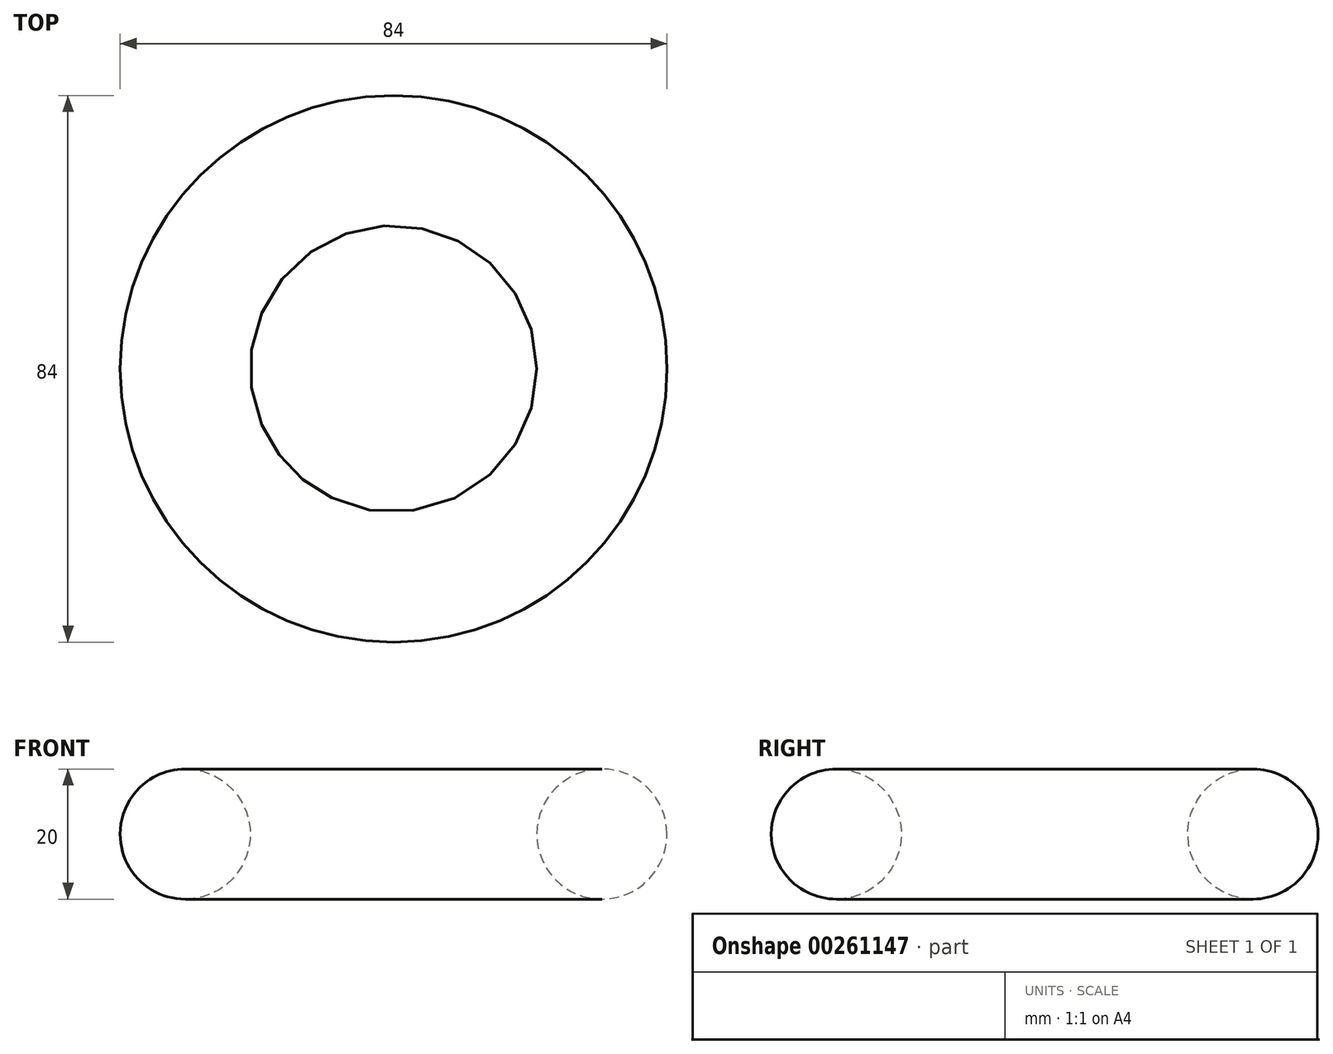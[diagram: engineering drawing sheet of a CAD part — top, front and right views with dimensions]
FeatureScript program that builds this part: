
annotation { "Feature Type Name" : "Feature", "Feature Type Description" : "" }
export const myFeature = defineFeature(function(context is Context, id is Id, definition is map)
    precondition{}
    {
        {
            var Q0;
            Q0=qCreatedBy(makeId("Front.planeOp"),FACE);
            var sketch = newSketch(context, id + "F0", { "sketchPlane" : qUnion([Q0])});
            skCircle(sketch, "E0", {"center": v(32, 0) * mm, "radius": 10 * mm});
            skLineSegment(sketch, "E1", {"start": v(0, 39.73) * mm, "end": v(0, -48.34) * mm, "construction": true});
            skSolve(sketch);
        }
        {
            var Q0;
            Q0=makeQuery(id+"F0.imprint","IMPRINT",FACE,{"disambiguationData":[TD([[makeQuery(id+"F0.imprint","IMPRINT",EDGE,{"derivedFrom":sQuery(id+"F0.wireOp",EDGE,"E0")}),1.0]])]});
            var Q1;
            Q1=sQuery(id+"F0.wireOp",EDGE,"E1");
            revolve(context, id + "F1", {"entities" : qUnion([Q0]), "axis" : qUnion([Q1]), "revolveType" : RevolveType.FULL});
        }
    });
